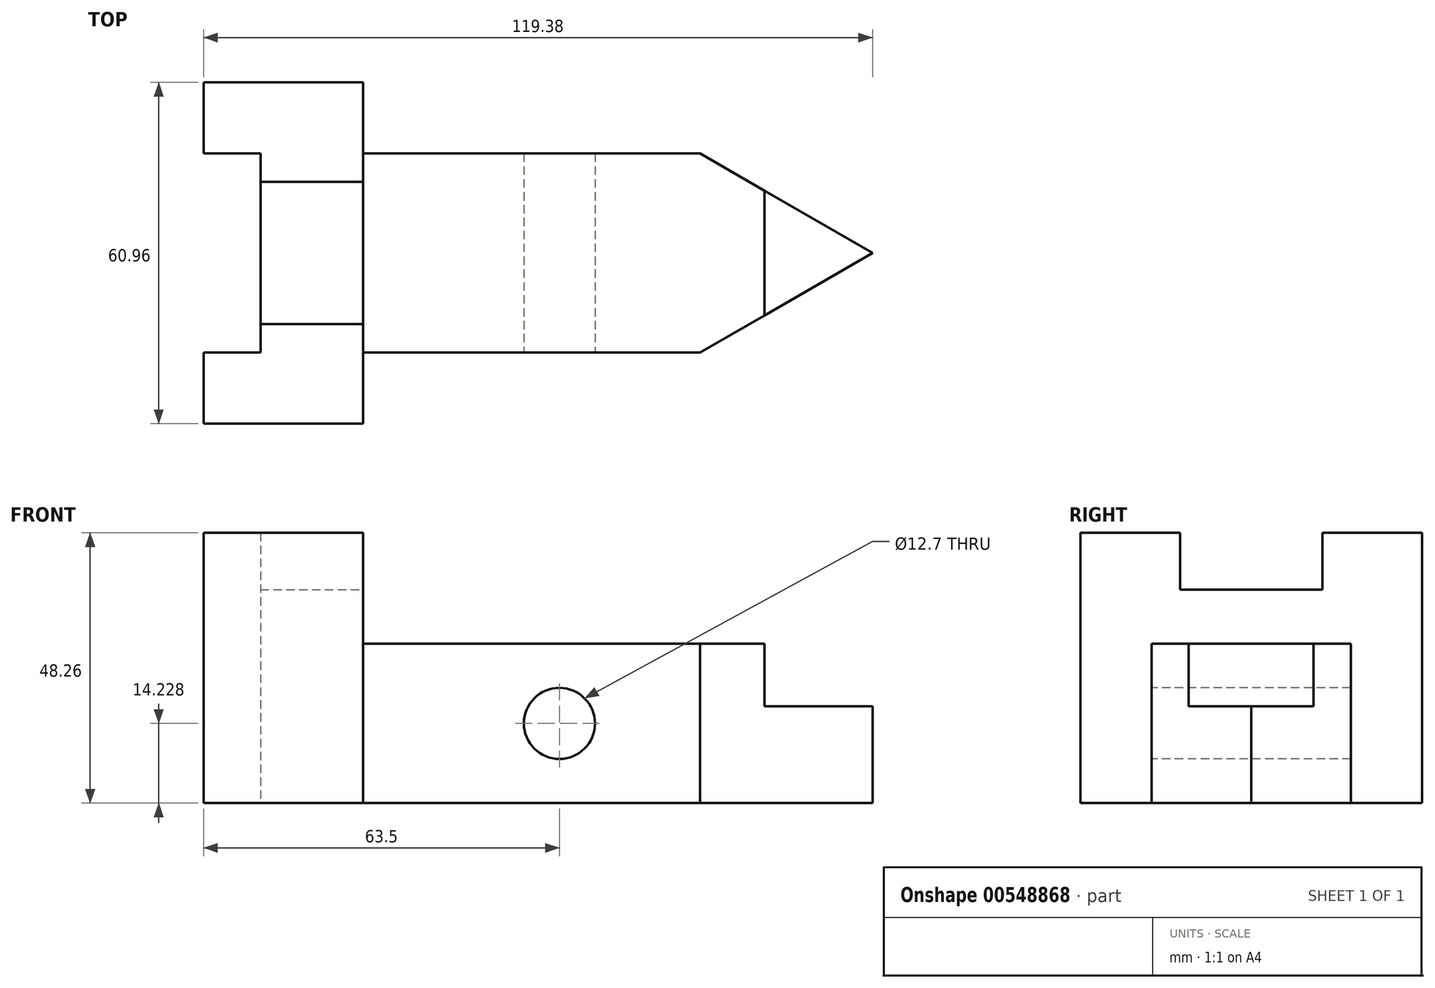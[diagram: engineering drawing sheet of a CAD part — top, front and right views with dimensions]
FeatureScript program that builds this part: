
annotation { "Feature Type Name" : "Feature", "Feature Type Description" : "" }
export const myFeature = defineFeature(function(context is Context, id is Id, definition is map)
    precondition{}
    {
        {
            var Q0;
            Q0=qCreatedBy(makeId("Right.planeOp"),FACE);
            var sketch = newSketch(context, id + "F0", { "sketchPlane" : qUnion([Q0])});
            skLineSegment(sketch, "E0.bottom", {"start": v(-32.79, 48.01) * mm, "end": v(28.17, 48.01) * mm});
            skLineSegment(sketch, "E0.top", {"start": v(-32.79, -0.25) * mm, "end": v(28.17, -0.25) * mm});
            skLineSegment(sketch, "E0.left", {"start": v(-32.79, 48.01) * mm, "end": v(-32.79, -0.25) * mm});
            skLineSegment(sketch, "E0.right", {"start": v(28.17, 48.01) * mm, "end": v(28.17, -0.25) * mm});
            skSolve(sketch);
        }
        {
            var Q0;
            Q0 = qSketchRegion(id + "F0", true);
            var Q1;
            Q1=makeQuery(id+"F0.imprint","IMPRINT",FACE,{"disambiguationData":[TD([[makeQuery(id+"F0.imprint","IMPRINT",EDGE,{"derivedFrom":sQuery(id+"F0.wireOp",EDGE,"E0.bottom")}),-1.0]])]});
            extrude(context, id + "F1", {"entities" : qUnion([Q0, Q1]), "depth" : 28.45 * mm, "offsetDistance" : 25.4 * mm});
        }
        {
            var Q0;
            Q0=makeQuery(id+"F1.opExtrude","CAP_FACE",FACE,{"disambiguationData":[OSD([sQuery(id+"F0.wireOp",EDGE,"E0.bottom"),sQuery(id+"F0.wireOp",EDGE,"E0.top"),sQuery(id+"F0.wireOp",EDGE,"E0.left"),sQuery(id+"F0.wireOp",EDGE,"E0.right")])],"isStart":false});
            var sketch = newSketch(context, id + "F2", { "sketchPlane" : qUnion([Q0])});
            skLineSegment(sketch, "E1.bottom", {"start": v(-15, 48.01) * mm, "end": v(10.4, 48.01) * mm});
            skLineSegment(sketch, "E1.top", {"start": v(-15, 37.85) * mm, "end": v(10.4, 37.85) * mm});
            skLineSegment(sketch, "E1.left", {"start": v(-15, 48.01) * mm, "end": v(-15, 37.85) * mm});
            skLineSegment(sketch, "E1.right", {"start": v(10.4, 48.01) * mm, "end": v(10.4, 37.85) * mm});
            skSolve(sketch);
        }
        {
            var Q0;
            Q0=makeQuery(id+"F2.imprint","IMPRINT",FACE,{"disambiguationData":[TD([[makeQuery(id+"F2.imprint","IMPRINT",EDGE,{"derivedFrom":sQuery(id+"F2.wireOp",EDGE,"E1.bottom")}),-1.0]])]});
            extrude(context, id + "F3", {"entities" : qUnion([Q0]), "operationType" : NewBodyOperationType.REMOVE, "oppositeDirection" : true, "depth" : 50.8 * mm, "offsetDistance" : 25.4 * mm});
        }
        {
            var Q0;
            Q0=makeQuery(id+"F1.opExtrude","CAP_FACE",FACE,{"disambiguationData":[OSD([sQuery(id+"F0.wireOp",EDGE,"E0.bottom"),sQuery(id+"F0.wireOp",EDGE,"E0.top"),sQuery(id+"F0.wireOp",EDGE,"E0.left"),sQuery(id+"F0.wireOp",EDGE,"E0.right")])],"isStart":true});
            var sketch = newSketch(context, id + "F4", { "sketchPlane" : qUnion([Q0])});
            skLineSegment(sketch, "E2.bottom", {"start": v(-15.47, 48.01) * mm, "end": v(20.09, 48.01) * mm});
            skLineSegment(sketch, "E2.top", {"start": v(-15.47, -0.25) * mm, "end": v(20.09, -0.25) * mm});
            skLineSegment(sketch, "E2.left", {"start": v(-15.47, 48.01) * mm, "end": v(-15.47, -0.25) * mm});
            skLineSegment(sketch, "E2.right", {"start": v(20.09, 48.01) * mm, "end": v(20.09, -0.25) * mm});
            skSolve(sketch);
        }
        {
            var Q0;
            Q0=makeQuery(id+"F4.imprint","IMPRINT",FACE,{"disambiguationData":[TD([[makeQuery(id+"F4.imprint","IMPRINT",EDGE,{"derivedFrom":sQuery(id+"F4.wireOp",EDGE,"E2.top")}),-1.0]])]});
            extrude(context, id + "F5", {"entities" : qUnion([Q0]), "operationType" : NewBodyOperationType.REMOVE, "oppositeDirection" : true, "depth" : 10.16 * mm, "offsetDistance" : 25.4 * mm});
        }
        {
            var Q0;
            Q0=makeQuery(id+"F1.opExtrude","CAP_FACE",FACE,{"disambiguationData":[OSD([sQuery(id+"F0.wireOp",EDGE,"E0.bottom"),sQuery(id+"F0.wireOp",EDGE,"E0.top"),sQuery(id+"F0.wireOp",EDGE,"E0.left"),sQuery(id+"F0.wireOp",EDGE,"E0.right")])],"isStart":false});
            var sketch = newSketch(context, id + "F6", { "sketchPlane" : qUnion([Q0])});
            skLineSegment(sketch, "E3.bottom", {"start": v(-20.09, -0.25) * mm, "end": v(15.47, -0.25) * mm});
            skLineSegment(sketch, "E3.top", {"start": v(-20.09, 28.2) * mm, "end": v(15.47, 28.2) * mm});
            skLineSegment(sketch, "E3.left", {"start": v(-20.09, -0.25) * mm, "end": v(-20.09, 28.2) * mm});
            skLineSegment(sketch, "E3.right", {"start": v(15.47, -0.25) * mm, "end": v(15.47, 28.2) * mm});
            skSolve(sketch);
        }
        {
            var Q0;
            Q0=makeQuery(id+"F6.imprint","IMPRINT",FACE,{"disambiguationData":[TD([[makeQuery(id+"F6.imprint","IMPRINT",EDGE,{"derivedFrom":sQuery(id+"F6.wireOp",EDGE,"E3.bottom")}),1.0]])]});
            extrude(context, id + "F7", {"entities" : qUnion([Q0]), "operationType" : NewBodyOperationType.ADD, "depth" : 90.93 * mm, "offsetDistance" : 25.4 * mm});
        }
        {
            var Q0;
            Q0=makeQuery(id+"F7.opExtrude","SWEPT_FACE",FACE,{"disambiguationData":[OSD([sQuery(id+"F6.wireOp",EDGE,"E3.top")])]});
            var sketch = newSketch(context, id + "F8", { "sketchPlane" : qUnion([Q0])});
            skLineSegment(sketch, "E4", {"start": v(119.38, -2.3) * mm, "end": v(119.38, -20.09) * mm});
            skLineSegment(sketch, "E5", {"start": v(119.38, -2.3) * mm, "end": v(88.58, -20.09) * mm});
            skLineSegment(sketch, "E6", {"start": v(119.38, -2.3) * mm, "end": v(88.58, 15.47) * mm});
            skSolve(sketch);
        }
        {
            var Q0;
            {var subQ0=sQuery(id+"F8.wireOp",EDGE,"E6");Q0=makeQuery(id+"F8.imprint","IMPRINT",FACE,{"disambiguationData":[TD([[makeQuery(id+"F8.imprint","IMPRINT",EDGE,{"derivedFrom":subQ0}),-1.0]])]});}
            var Q1;
            {var subQ0=sQuery(id+"F8.wireOp",EDGE,"E4");Q1=makeQuery(id+"F8.imprint","IMPRINT",FACE,{"disambiguationData":[TD([[makeQuery(id+"F8.imprint","IMPRINT",EDGE,{"derivedFrom":subQ0}),1.0]])]});}
            extrude(context, id + "F9", {"entities" : qUnion([Q0, Q1]), "operationType" : NewBodyOperationType.REMOVE, "oppositeDirection" : true, "depth" : 50.8 * mm, "offsetDistance" : 25.4 * mm});
        }
        {
            var Q0;
            Q0=makeQuery(id+"F7.opExtrude","SWEPT_FACE",FACE,{"disambiguationData":[OSD([sQuery(id+"F6.wireOp",EDGE,"E3.top")])]});
            var sketch = newSketch(context, id + "F10", { "sketchPlane" : qUnion([Q0])});
            skLineSegment(sketch, "E7", {"start": v(119.38, -2.3) * mm, "end": v(100.08, -2.3) * mm});
            skLineSegment(sketch, "E8", {"start": v(100.08, -2.3) * mm, "end": v(100.08, -13.46) * mm});
            skLineSegment(sketch, "E9", {"start": v(100.08, -13.46) * mm, "end": v(100.08, 8.84) * mm});
            skSolve(sketch);
        }
        {
            var Q0;
            {var subQ0=sQuery(id+"F10.wireOp",EDGE,"E7");Q0=makeQuery(id+"F10.imprint","IMPRINT",FACE,{"disambiguationData":[TD([[makeQuery(id+"F10.imprint","IMPRINT",EDGE,{"derivedFrom":subQ0}),-1.0]])]});}
            var Q1;
            {var subQ0=sQuery(id+"F10.wireOp",EDGE,"E7");Q1=makeQuery(id+"F10.imprint","IMPRINT",FACE,{"disambiguationData":[TD([[makeQuery(id+"F10.imprint","IMPRINT",EDGE,{"derivedFrom":subQ0}),1.0]])]});}
            extrude(context, id + "F11", {"entities" : qUnion([Q0, Q1]), "operationType" : NewBodyOperationType.REMOVE, "oppositeDirection" : true, "depth" : 11.18 * mm, "offsetDistance" : 25.4 * mm});
        }
        {
            var Q0;
            Q0=makeQuery(id+"F7.opExtrude","SWEPT_FACE",FACE,{"disambiguationData":[OSD([sQuery(id+"F6.wireOp",EDGE,"E3.left")])]});
            var sketch = newSketch(context, id + "F12", { "sketchPlane" : qUnion([Q0])});
            skPoint(sketch, "E10", {"position": v(63.5, 13.98) * mm});
            skCircle(sketch, "E11", {"center": v(63.5, 13.98) * mm, "radius": 6.35 * mm});
            skSolve(sketch);
        }
        {
            var Q0;
            Q0=makeQuery(id+"F12.imprint","IMPRINT",FACE,{"disambiguationData":[TD([[makeQuery(id+"F12.imprint","IMPRINT",EDGE,{"derivedFrom":sQuery(id+"F12.wireOp",EDGE,"E11")}),1.0]])]});
            extrude(context, id + "F13", {"entities" : qUnion([Q0]), "operationType" : NewBodyOperationType.REMOVE, "oppositeDirection" : true, "depth" : 35.81 * mm, "offsetDistance" : 25.4 * mm});
        }
    });
